# Revit family: RN 82036 Optipress-Segment de tuyau
name_source: partatom
category: Rohrformteile
units: mm (PartAtom-declared; Revit-internal decimal feet)

## family parameters
Arbeitsebenenbasiert = Nein
Beim Laden mit Abzugskörper schneiden = Nein
Bemaßung runder Anschluss = Durchmesser verwenden
Gemeinsam genutzt = Nein
Immer vertikal = Ja
Teiletyp = Nicht definiert

## types (4) — shared parameters
1.010.00.2 Numéro de feuille de la directive = 29
1.010.00.3 Date de publication (mois) de la ligne directrice = 201308
1.010.00.4 Nom du Fabricant = R. Nussbaum AG
1.010.00.5 Date de révision du fichier = 20190521
1.010.00.6 Adresse Web du fabricant = http://www.nussbaum.ch
1.100.00.4 Désignation du produit = Alimentation
1.110.00.2 Indice = 4
1.110.00.4 Désignation du produit = Optipress
1.960/3L.00.8 Lien (URL) = https://www.nussbaum.ch
29.700.00.4 Nom du produit = Optipress-Segment de tuyau, pour robinets de distribution à sertir
29.700.00.5 Identification du produit = 2
29.700.00.6 Forme transversale = 1
29.700.00.7 Système de taille nominale = DN
29.700.00.8 Système de pression nominale = PN
29.710.02.4 Pression nominale = 16
29.710.02.5 Max. [hPa] = 1600
29.710.02.7 Max. [hPa] = 1600
29.710.02.9 Max. [°C] = 95
CONNECTOR1_dX_01 = 100 mm  [stored 0.328084 ft]
Connector Visibility = Nein
EnclosingSpace Visibility = Nein

## per-type parameters (varying)
| type | 1.800.00.3 Numéro BS | 1.810.00.3 Numéro de commande fabricant | 1.810.00.4 Numéro DATANORM | 1.810.00.6 Numéro GTIN | 29.710.02.10 Poids d'ajustement [kg] | 29.710.02.3 La désignation | CONNECTOR0_DIAMETER_dX_0r | CONNECTOR0_dX_01 | CONNECTOR0_ref_dX | CONNECTOR1_DIAMETER_dX_0r | CONNECTOR1_dX_00 | CONNECTOR1_ref_dX | R. Nussbaum AG 82036.25 fr Visibility | R. Nussbaum AG 82036.26 fr Visibility | R. Nussbaum AG 82036.27 fr Visibility | R. Nussbaum AG 82036.28 fr Visibility |
| 82036.25, Optipress-Segment de tuyau, pour robinets de distribution à sertir, DN=25, L=100 | 01900400000000000000000000000000000000000000000062000000000000000001 | 82036.25 | 82036.25 | 7612945689795 | 0.076 | Optipress-Segment de tuyau, pour robinets de distribution à sertir, DN=25, L=100 | 25 mm  [stored 0.082021 ft] | 24 mm | 24 mm | 25 mm  [stored 0.082021 ft] | 76 mm | 76 mm | Ja | Nein | Nein | Nein |
| 82036.26, Optipress-Segment de tuyau, pour robinets de distribution à sertir, DN=32, L=100 | 01900400000000000000000000000000000000000000000062000000000000000002 | 82036.26 | 82036.26 | 7612945689801 | 0.12 | Optipress-Segment de tuyau, pour robinets de distribution à sertir, DN=32, L=100 | 32 mm | 26 mm  [stored 0.0853018 ft] | 26 mm  [stored 0.0853018 ft] | 32 mm | 74 mm | 74 mm | Nein | Ja | Nein | Nein |
| 82036.27, Optipress-Segment de tuyau, pour robinets de distribution à sertir, DN=40, L=100 | 01900400000000000000000000000000000000000000000062000000000000000003 | 82036.27 | 82036.27 | 7612945689818 | 0.149 | Optipress-Segment de tuyau, pour robinets de distribution à sertir, DN=40, L=100 | 40 mm | 36 mm | 36 mm | 40 mm | 64 mm | 64 mm | Nein | Nein | Ja | Nein |
| 82036.28, Optipress-Segment de tuyau, pour robinets de distribution à sertir, DN=50, L=100 | 01900400000000000000000000000000000000000000000062000000000000000004 | 82036.28 | 82036.28 | 7612945689825 | 0.186 | Optipress-Segment de tuyau, pour robinets de distribution à sertir, DN=50, L=100 | 50 mm  [stored 0.164042 ft] | 40 mm | 40 mm | 50 mm  [stored 0.164042 ft] | 60 mm | 60 mm | Nein | Nein | Nein | Ja |

note: column(s) folded — value = type name in every type: 1.800.00.4 Champ de commentaires

note: [stored X ft] marks values corroborated as IEEE doubles in the binary element streams (Revit-internal decimal feet)

## geometry (parser evidence)
native form markers: Sweep x2
no freeform markers — native parametric forms only
